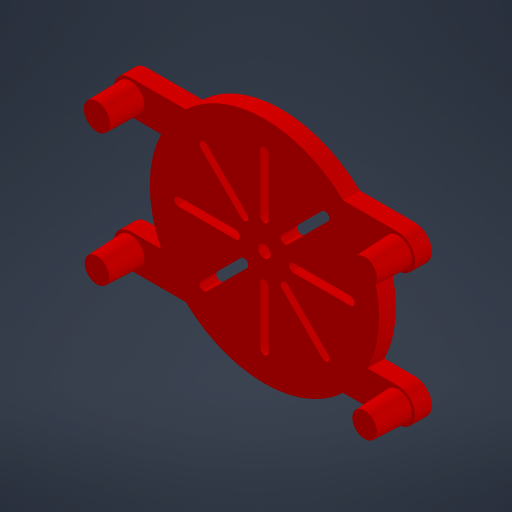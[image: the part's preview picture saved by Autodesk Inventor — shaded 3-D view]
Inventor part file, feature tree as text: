
AUTODESK INVENTOR PART (.ipt)
format: ipt  version: 2023.4 (Build 274418000, 418)  size: 304,128 bytes
history: native  units: mm
features: chamfer x4, other x3, extrude x2, reference x2
ambient origin geometry x8: Origin, YZ Plane, XZ Plane, XY Plane, X Axis, Y Axis, Z Axis, Center Point
bodies: Solid1 (feature_tree)
feature tree (11):
  extrude  "Extrusion2"  Depth=2.5mm TaperAngle=0.0deg
  extrude  "Extrusion3"  Depth=5.0mm TaperAngle=0.0deg
  chamfer  "Chamfer1"  Distance=5.0mm
  chamfer  "Chamfer2"  Distance=5.0mm
  chamfer  "Chamfer3"  Distance=5.0mm
  chamfer  "Chamfer4"  Distance=5.0mm
  reference  "Reference14"
  reference  "Reference15"
  other  "<path>\Projects\Project Protocube\Protocube\CAD, STL, OBJ Files\1 CAD\Cube 1x1 V5.iam"
  other  "Cube 1x1 V5.iam"
  other  "Cube 1x1 Bottom V5 Closed:1"
note: 1 file-system path scrubbed to <path> (originals preserved in map.json)
